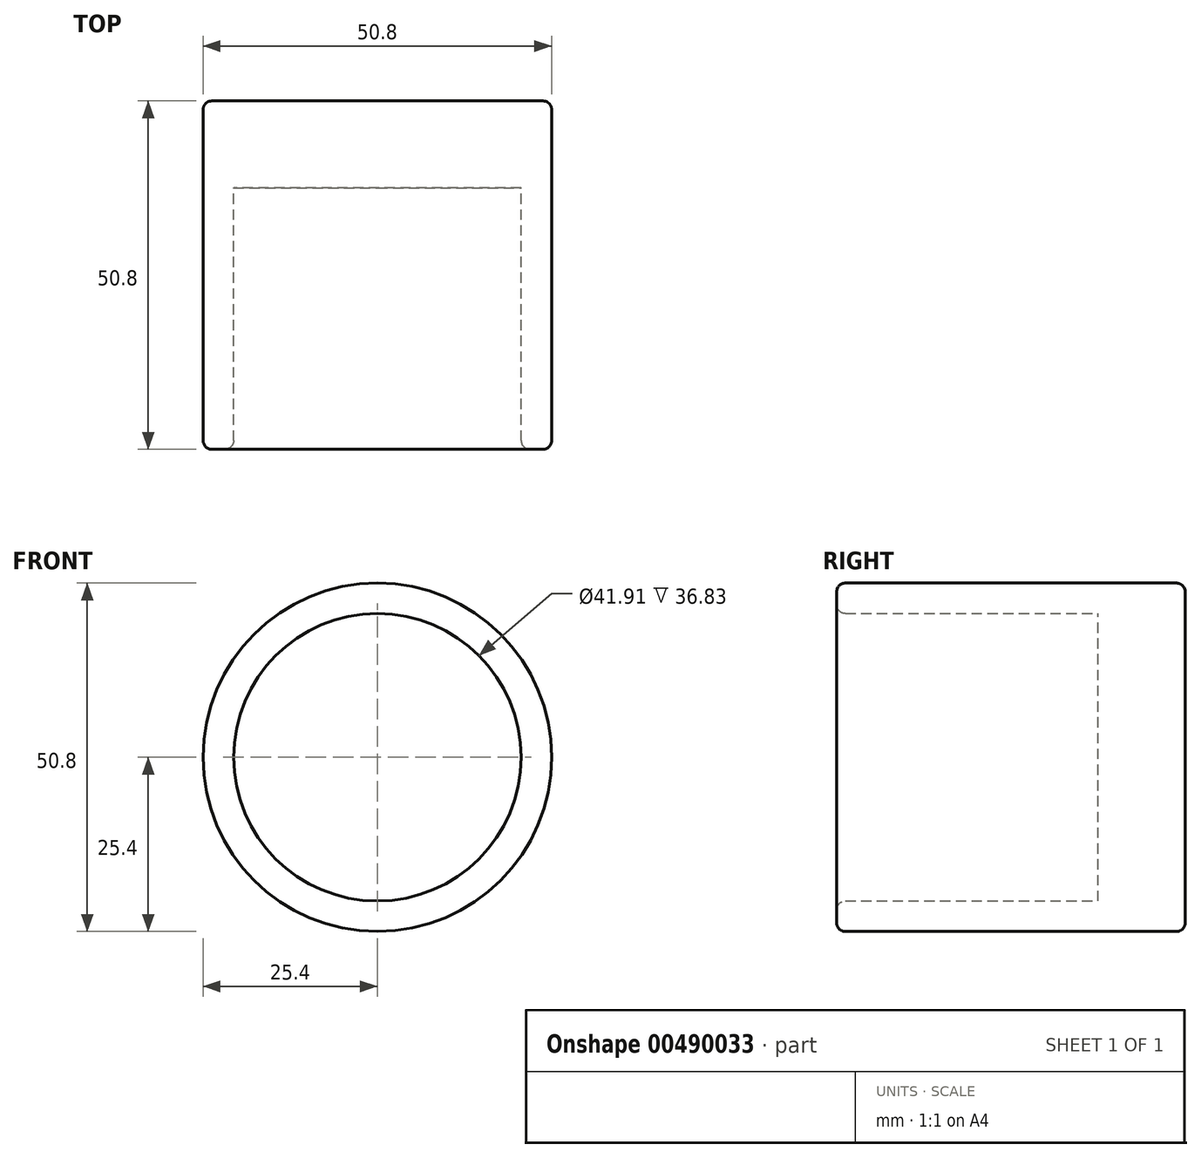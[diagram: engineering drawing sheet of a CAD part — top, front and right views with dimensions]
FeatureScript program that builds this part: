
annotation { "Feature Type Name" : "Feature", "Feature Type Description" : "" }
export const myFeature = defineFeature(function(context is Context, id is Id, definition is map)
    precondition{}
    {
        {
            var Q0;
            Q0=qCreatedBy(makeId("Front.planeOp"),FACE);
            var sketch = newSketch(context, id + "F0", { "sketchPlane" : qUnion([Q0])});
            skCircle(sketch, "E0", {"center": v(0, 0) * mm, "radius": 25.4 * mm});
            skCircle(sketch, "E1", {"center": v(0, 0) * mm, "radius": 20.96 * mm});
            skSolve(sketch);
        }
        {
            var Q0;
            Q0=makeQuery(id+"F0.imprint","IMPRINT",FACE,{"disambiguationData":[TD([[makeQuery(id+"F0.imprint","IMPRINT",EDGE,{"derivedFrom":sQuery(id+"F0.wireOp",EDGE,"E1")}),1.0]])]});
            var sketch = newSketch(context, id + "F1", { "sketchPlane" : qUnion([Q0])});
            skSolve(sketch);
        }
        {
            var Q0;
            Q0=makeQuery(id+"F0.imprint","IMPRINT",FACE,{"disambiguationData":[TD([[makeQuery(id+"F0.imprint","IMPRINT",EDGE,{"derivedFrom":sQuery(id+"F0.wireOp",EDGE,"E0")}),1.0]])]});
            extrude(context, id + "F2", {"entities" : qUnion([Q0]), "depth" : 50.8 * mm});
        }
        {
            var Q0;
            Q0=makeQuery(id+"F1.imprint","IMPRINT",FACE,{"disambiguationData":[TD([[makeQuery(id+"F1.imprint","IMPRINT",EDGE,{"derivedFrom":makeQuery(id+"F0.imprint","IMPRINT",EDGE,{"derivedFrom":sQuery(id+"F0.wireOp",EDGE,"E1")})}),1.0]])]});
            extrude(context, id + "F3", {"entities" : qUnion([Q0]), "operationType" : NewBodyOperationType.ADD, "depth" : 12.7 * mm});
        }
        {
            var Q0;
            Q0=makeQuery(id+"F2.opExtrude","CAP_EDGE",EDGE,{"disambiguationData":[OSD([sQuery(id+"F0.wireOp",EDGE,"E0")])],"isStart":false});
            fillet(context, id + "F4", {"entities" : qUnion([Q0]), "radius" : 1.27 * mm, "tangentPropagation" : true, "allowEdgeOverflow" : false});
        }
        {
            var Q0;
            Q0=makeQuery(id+"F2.opExtrude","CAP_EDGE",EDGE,{"disambiguationData":[OSD([sQuery(id+"F0.wireOp",EDGE,"E1")])],"isStart":false});
            fillet(context, id + "F5", {"entities" : qUnion([Q0]), "radius" : 1.27 * mm, "tangentPropagation" : true, "allowEdgeOverflow" : false});
        }
        {
            var Q0;
            Q0=makeQuery(id+"F2.opExtrude","CAP_EDGE",EDGE,{"disambiguationData":[OSD([sQuery(id+"F0.wireOp",EDGE,"E0")])],"isStart":true});
            fillet(context, id + "F6", {"entities" : qUnion([Q0]), "radius" : 1.27 * mm, "tangentPropagation" : true, "allowEdgeOverflow" : false});
        }
    });
